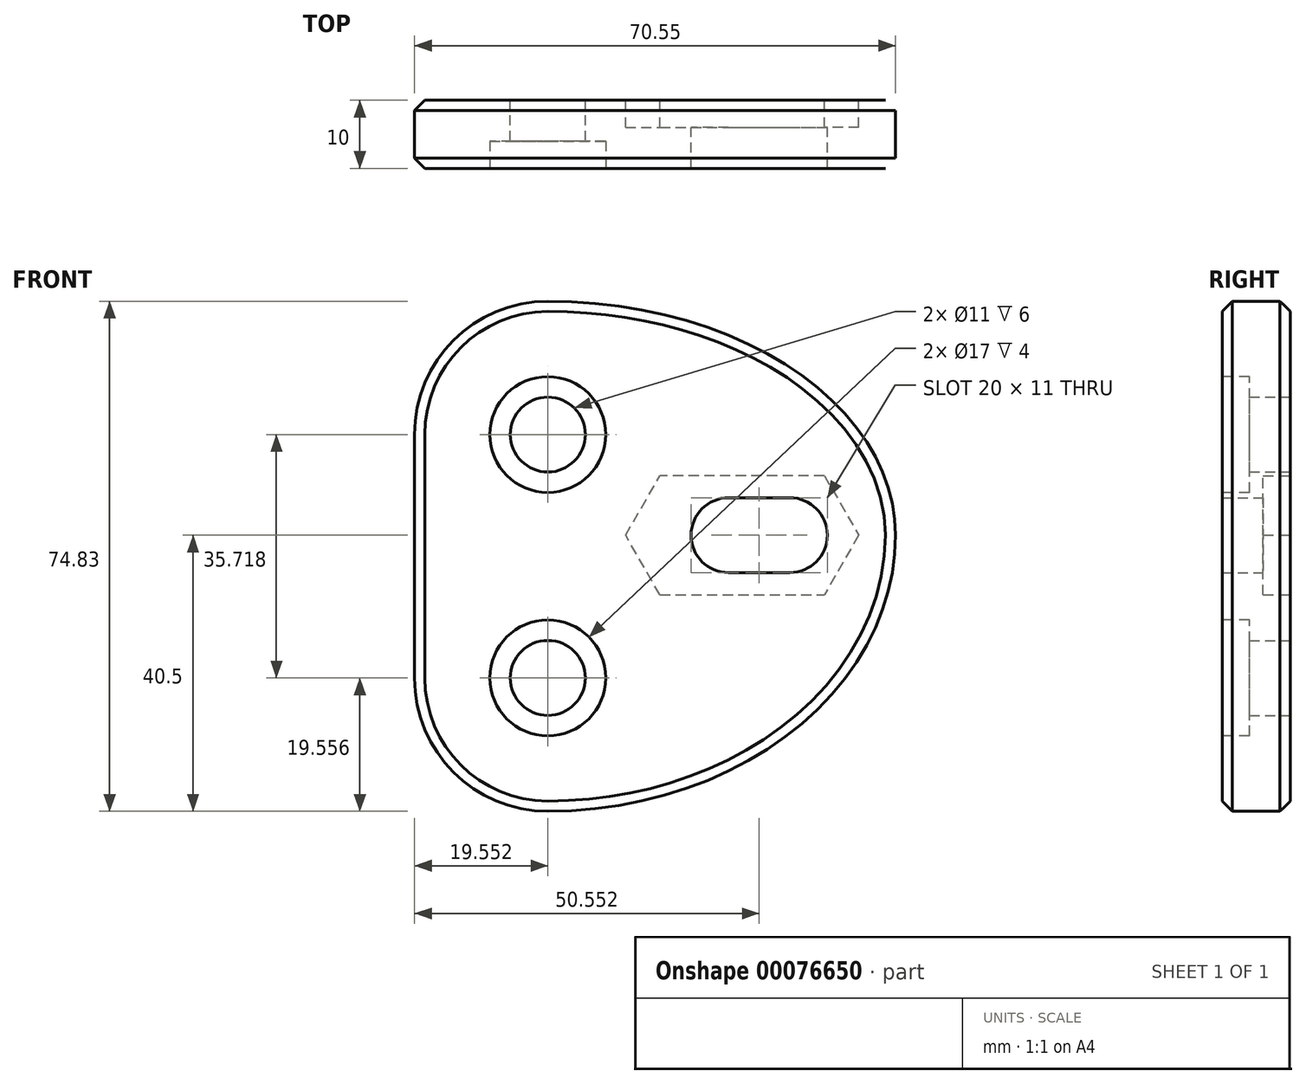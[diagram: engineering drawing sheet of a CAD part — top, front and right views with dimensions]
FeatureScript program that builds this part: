
annotation { "Feature Type Name" : "Feature", "Feature Type Description" : "" }
export const myFeature = defineFeature(function(context is Context, id is Id, definition is map)
    precondition{}
    {
        {
            var Q0;
            Q0=qCreatedBy(makeId("Front.planeOp"),FACE);
            var sketch = newSketch(context, id + "F0", { "sketchPlane" : qUnion([Q0])});
            skLineSegment(sketch, "E0.left", {"start": v(-80.6, 14.77) * mm, "end": v(-80.6, -20.94) * mm});
            skArc(sketch, "E1.filletArc", {"start": v(-61.04, 34.33) * mm, "mid": v(-74.87, 28.6) * mm, "end": v(-80.6, 14.77) * mm});
            skArc(sketch, "E2.filletArc", {"start": v(-80.6, -20.94) * mm, "mid": v(-74.87, -34.77) * mm, "end": v(-61.04, -40.5) * mm});
            skCircle(sketch, "E3", {"center": v(-61.04, -20.94) * mm, "radius": 5.5 * mm});
            skCircle(sketch, "E4", {"center": v(-61.04, 14.77) * mm, "radius": 5.5 * mm});
            skArc(sketch, "E5", {"start": v(-25.54, -5.5) * mm, "mid": v(-20.04, 0) * mm, "end": v(-25.54, 5.5) * mm});
            skArc(sketch, "E6", {"start": v(-34.54, 5.5) * mm, "mid": v(-40.04, 0) * mm, "end": v(-34.54, -5.5) * mm});
            skLineSegment(sketch, "E7", {"start": v(-40.04, 0) * mm, "end": v(-20.04, 0) * mm});
            skLineSegment(sketch, "E8", {"start": v(-34.54, 5.5) * mm, "end": v(-25.54, 5.5) * mm});
            skLineSegment(sketch, "E9", {"start": v(-25.54, -5.5) * mm, "end": v(-34.54, -5.5) * mm});
            skLineSegment(sketch, "E10", {"start": v(-20.04, 0) * mm, "end": v(-10.04, 0) * mm});
            skEllipticalArc(sketch, "E11.trimOffspring", {});
            skEllipticalArc(sketch, "E12", {});
            const initialGuessF0  = {"E11.trimOffspring": [-0.061037882258116044, 0, 0, 1, 0.03433, 0.051, 4.71238898038469, 6.283185307179586], "E12": [-0.061037882258116044, 0, 0, -1, 0.0405, 0.051, 6.283185307179586, 1.5707963267948966]};
            skSetInitialGuess(sketch, initialGuessF0);
            skSolve(sketch);
        }
        {
            var Q0;
            Q0=makeQuery(id+"F0.imprint","IMPRINT",FACE,{"disambiguationData":[TD([[makeQuery(id+"F0.imprint","IMPRINT",EDGE,{"derivedFrom":sQuery(id+"F0.wireOp",EDGE,"E0.left")}),1.0]])]});
            extrude(context, id + "F1", {"entities" : qUnion([Q0]), "depth" : 10 * mm});
        }
        {
            var Q0;
            Q0=makeQuery(id+"F1.opExtrude","CAP_FACE",FACE,{"disambiguationData":[OSD([sQuery(id+"F0.wireOp",EDGE,"E0.left"),sQuery(id+"F0.wireOp",EDGE,"E1.filletArc"),sQuery(id+"F0.wireOp",EDGE,"E2.filletArc"),sQuery(id+"F0.wireOp",EDGE,"E3"),sQuery(id+"F0.wireOp",EDGE,"E4"),sQuery(id+"F0.wireOp",EDGE,"E5"),sQuery(id+"F0.wireOp",EDGE,"E6"),sQuery(id+"F0.wireOp",EDGE,"E8"),sQuery(id+"F0.wireOp",EDGE,"E9"),sQuery(id+"F0.wireOp",EDGE,"E11.trimOffspring"),sQuery(id+"F0.wireOp",EDGE,"E12")])],"isStart":false});
            var sketch = newSketch(context, id + "F2", { "sketchPlane" : qUnion([Q0])});
            skCircle(sketch, "E13", {"center": v(-61.04, 14.77) * mm, "radius": 8.5 * mm});
            skCircle(sketch, "E14", {"center": v(-61.04, -20.94) * mm, "radius": 8.5 * mm});
            skSolve(sketch);
        }
        {
            var Q0;
            Q0 = qSketchRegion(id + "F2", true);
            extrude(context, id + "F3", {"entities" : qUnion([Q0]), "operationType" : NewBodyOperationType.REMOVE, "oppositeDirection" : true, "depth" : 4 * mm});
        }
        {
            var Q0;
            Q0=makeQuery(id+"F0.imprint","IMPRINT",FACE,{"disambiguationData":[TD([[makeQuery(id+"F0.imprint","IMPRINT",EDGE,{"derivedFrom":sQuery(id+"F0.wireOp",EDGE,"E0.left")}),1.0]])]});
            var sketch = newSketch(context, id + "F4", { "sketchPlane" : qUnion([Q0])});
            skLineSegment(sketch, "E15.1", {"start": v(-20.49, 8.75) * mm, "end": v(-15.43, 0) * mm});
            skLineSegment(sketch, "E15.2", {"start": v(-15.43, 0) * mm, "end": v(-20.49, -8.75) * mm});
            skLineSegment(sketch, "E16.4", {"start": v(-44.59, -8.75) * mm, "end": v(-49.64, 0) * mm});
            skLineSegment(sketch, "E16.5", {"start": v(-49.64, 0) * mm, "end": v(-44.59, 8.75) * mm});
            skLineSegment(sketch, "E17", {"start": v(-20.49, 8.75) * mm, "end": v(-44.59, 8.75) * mm});
            skLineSegment(sketch, "E18", {"start": v(-44.59, -8.75) * mm, "end": v(-20.49, -8.75) * mm});
            skPoint(sketch, "E19", {"position": v(-20.08, 0) * mm});
            skSolve(sketch);
        }
        {
            var Q0;
            Q0=makeQuery(id+"F4.imprint","IMPRINT",FACE,{"disambiguationData":[TD([[makeQuery(id+"F4.imprint","IMPRINT",EDGE,{"derivedFrom":sQuery(id+"F4.wireOp",EDGE,"E15.1")}),-1.0]])]});
            extrude(context, id + "F5", {"entities" : qUnion([Q0]), "operationType" : NewBodyOperationType.REMOVE, "depth" : 4 * mm});
        }
        {
            var Q0;
            Q0=makeQuery(id+"F1.opExtrude","CAP_EDGE",EDGE,{"disambiguationData":[OSD([sQuery(id+"F0.wireOp",EDGE,"E1.filletArc")])],"isStart":false});
            var Q1;
            Q1=makeQuery(id+"F1.opExtrude","CAP_EDGE",EDGE,{"disambiguationData":[OSD([sQuery(id+"F0.wireOp",EDGE,"E1.filletArc")])],"isStart":true});
            chamfer(context, id + "F6", {"entities" : qUnion([Q0, Q1]), "width" : 1.5 * mm, "tangentPropagation" : true});
        }
    });
